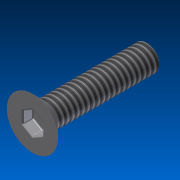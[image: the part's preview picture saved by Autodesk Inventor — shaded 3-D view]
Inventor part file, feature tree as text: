
AUTODESK INVENTOR PART (.ipt)
format: ipt  version: 2013 (Build 170138000, 138)  size: 166,400 bytes
history: native  units: mm
features: sketch x3, extrude x2, other x1, revolve x1, chamfer x1, fillet x1, thread x1
ambient origin geometry x1: Origin
feature tree (10):
  other  "ソリッド1"
  revolve  "回転1"
  extrude  "押し出し1"  TaperAngle=45.0deg  [1 undecoded]
  extrude  "押し出し2"  Depth=2.0mm
  chamfer  "面取り1"  Distance=1.0mm
  fillet  "フィレット1"  [1 undecoded]
  thread  "ねじ1"
  sketch  "スケッチ1"
  sketch  "スケッチ2"
  sketch  "スケッチ3"
note: 2 required parameter values undecoded (feature->parameter linkage not recoverable at this tier; creation-order binding heuristic only, values carry confidence <= 0.55)
